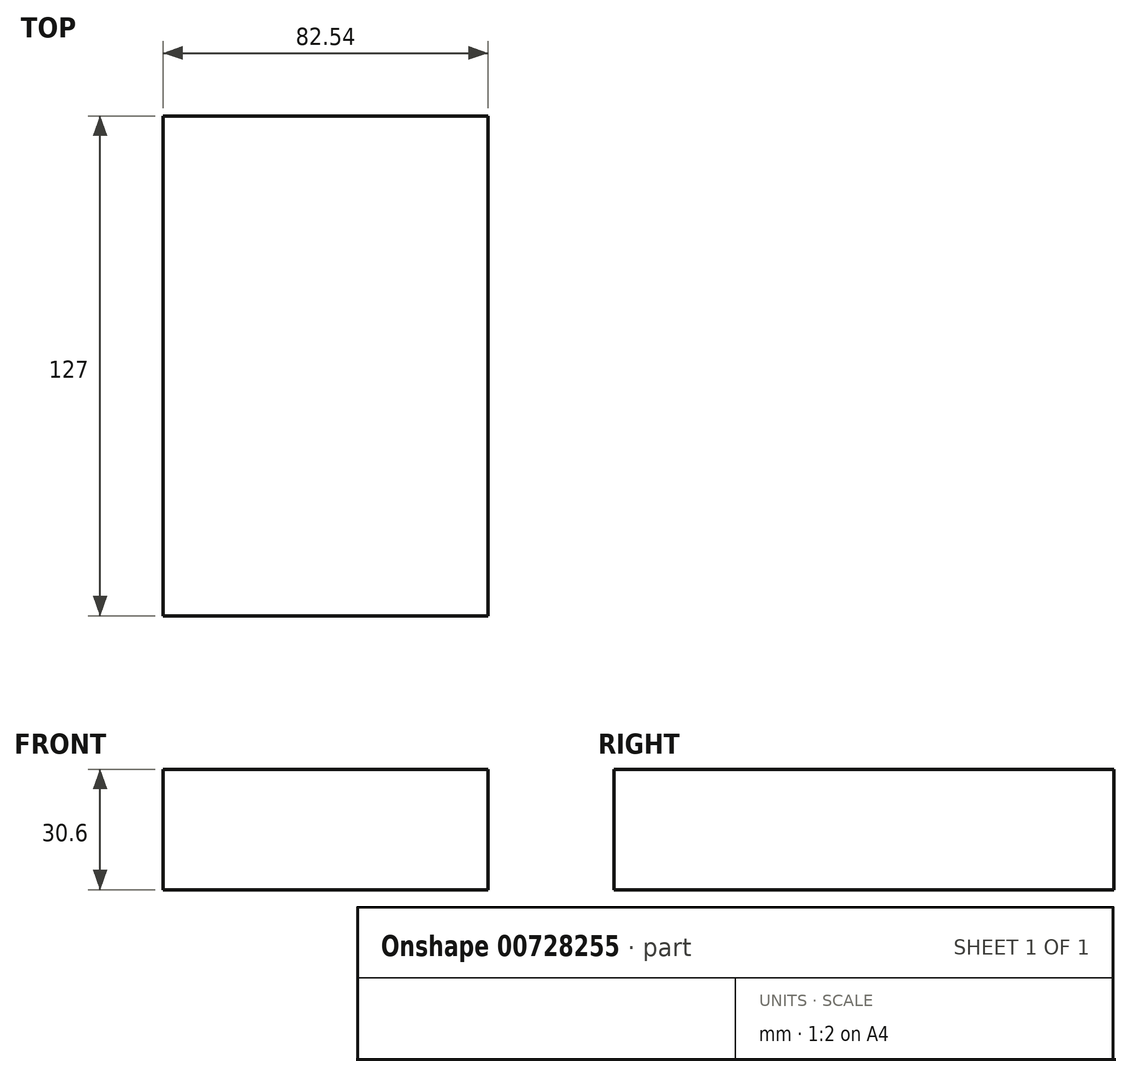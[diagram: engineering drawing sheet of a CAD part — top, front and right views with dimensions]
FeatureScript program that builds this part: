
annotation { "Feature Type Name" : "Feature", "Feature Type Description" : "" }
export const myFeature = defineFeature(function(context is Context, id is Id, definition is map)
    precondition{}
    {
        {
            var Q0;
            Q0=qCreatedBy(makeId("Front.planeOp"),FACE);
            var sketch = newSketch(context, id + "F0", { "sketchPlane" : qUnion([Q0])});
            skLineSegment(sketch, "E0.bottom", {"start": v(41.28, -15.3) * mm, "end": v(-41.28, -15.3) * mm});
            skLineSegment(sketch, "E0.top", {"start": v(41.28, 15.3) * mm, "end": v(-41.28, 15.3) * mm});
            skLineSegment(sketch, "E0.left", {"start": v(41.28, -15.3) * mm, "end": v(41.28, 15.3) * mm});
            skLineSegment(sketch, "E0.right", {"start": v(-41.28, -15.3) * mm, "end": v(-41.28, 15.3) * mm});
            skPoint(sketch, "E0.middle", {"position": v(0, 0) * mm});
            skLineSegment(sketch, "E1.bottom", {"start": v(54.77, 43.16) * mm, "end": v(107.78, 43.16) * mm});
            skLineSegment(sketch, "E1.top", {"start": v(54.77, 90.07) * mm, "end": v(107.78, 90.07) * mm});
            skLineSegment(sketch, "E1.left", {"start": v(54.77, 43.16) * mm, "end": v(54.77, 90.07) * mm});
            skLineSegment(sketch, "E1.right", {"start": v(107.78, 43.16) * mm, "end": v(107.78, 90.07) * mm});
            skPoint(sketch, "E1.middle", {"position": v(81.28, 66.61) * mm});
            skLineSegment(sketch, "E2", {"start": v(41.28, 15.3) * mm, "end": v(41.28, 41.05) * mm});
            skArc(sketch, "E3", {"start": v(41.28, 41.05) * mm, "mid": v(45.9, 52.2) * mm, "end": v(57.06, 56.83) * mm});
            skLineSegment(sketch, "E4", {"start": v(57.06, 56.83) * mm, "end": v(80.06, 56.83) * mm});
            skLineSegment(sketch, "E5.0", {"start": v(57.06, 66.86) * mm, "end": v(80.06, 66.86) * mm});
            skArc(sketch, "E5.1", {"start": v(31.24, 41.05) * mm, "mid": v(38.8, 59.3) * mm, "end": v(57.06, 66.86) * mm});
            skLineSegment(sketch, "E5.2", {"start": v(31.24, 15.3) * mm, "end": v(31.24, 41.05) * mm});
            skSolve(sketch);
        }
        {
            var Q0;
            Q0=makeQuery(id+"F0.imprint","IMPRINT",FACE,{"disambiguationData":[TD([[makeQuery(id+"F0.imprint","IMPRINT",EDGE,{"derivedFrom":sQuery(id+"F0.wireOp",EDGE,"E0.bottom")}),-1.0]])]});
            extrude(context, id + "F1", {"entities" : qUnion([Q0]), "endBound" : BoundingType.SYMMETRIC, "depth" : 127 * mm, "offsetDistance" : 25.4 * mm});
        }
    });
